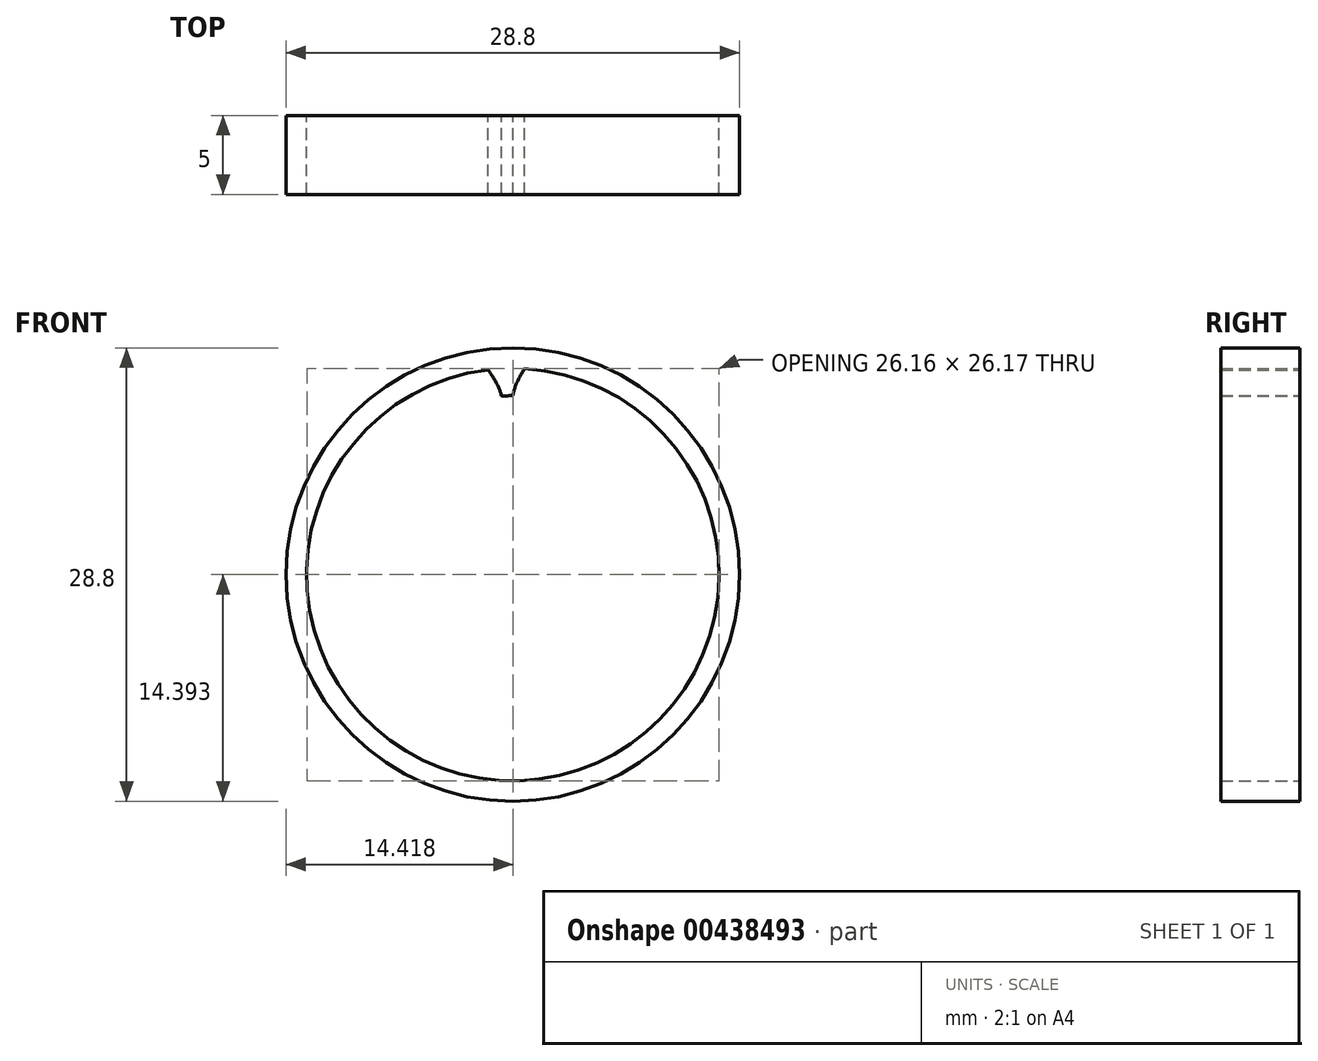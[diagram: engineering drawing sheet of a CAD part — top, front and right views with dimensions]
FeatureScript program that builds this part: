
annotation { "Feature Type Name" : "Feature", "Feature Type Description" : "" }
export const myFeature = defineFeature(function(context is Context, id is Id, definition is map)
    precondition{}
    {
        {
            var Q0;
            Q0=qCreatedBy(makeId("Front.planeOp"),FACE);
            var sketch = newSketch(context, id + "F0", { "sketchPlane" : qUnion([Q0])});
            skCircle(sketch, "E0", {"center": v(0, 0) * mm, "radius": 11.28 * mm, "construction": true});
            skLineSegment(sketch, "E1", {"start": v(1.96, 11.1) * mm, "end": v(0.02, 11.45) * mm, "construction": true});
            skLineSegment(sketch, "E2", {"start": v(0, 0) * mm, "end": v(0, 11.28) * mm, "construction": true});
            skLineSegment(sketch, "E3", {"start": v(1.96, 11.1) * mm, "end": v(0, 0) * mm, "construction": true});
            skLineSegment(sketch, "E4", {"start": v(0, 0) * mm, "end": v(3.86, 10.6) * mm, "construction": true});
            skLineSegment(sketch, "E5", {"start": v(3.86, 10.6) * mm, "end": v(2, 11.27) * mm, "construction": true});
            skLineSegment(sketch, "E6", {"start": v(0, 0) * mm, "end": v(5.64, 9.77) * mm, "construction": true});
            skLineSegment(sketch, "E7", {"start": v(5.64, 9.77) * mm, "end": v(3.93, 10.75) * mm, "construction": true});
            skLineSegment(sketch, "E8", {"start": v(0, 0) * mm, "end": v(7.25, 8.64) * mm, "construction": true});
            skLineSegment(sketch, "E9", {"start": v(7.25, 8.64) * mm, "end": v(5.74, 9.9) * mm, "construction": true});
            skLineSegment(sketch, "E10", {"start": v(2, 11.27) * mm, "end": v(0.16, 11.94) * mm, "construction": true});
            skLineSegment(sketch, "E11", {"start": v(3.93, 10.75) * mm, "end": v(2.23, 11.73) * mm, "construction": true});
            skLineSegment(sketch, "E12", {"start": v(2.23, 11.73) * mm, "end": v(0.52, 12.72) * mm, "construction": true});
            skLineSegment(sketch, "E13", {"start": v(5.74, 9.9) * mm, "end": v(4.23, 11.17) * mm, "construction": true});
            skLineSegment(sketch, "E14", {"start": v(4.23, 11.17) * mm, "end": v(2.73, 12.43) * mm, "construction": true});
            skLineSegment(sketch, "E15", {"start": v(2.73, 12.43) * mm, "end": v(1.22, 13.7) * mm, "construction": true});
            skFitSpline(sketch, "E16", {"points": [v(1.22, 13.7) * mm, v(0.52, 12.72) * mm, v(0.16, 11.94) * mm, v(0.02, 11.45) * mm, v(0, 11.28) * mm], "startDerivative": vector(-2.58, -3.18) * mm, "endDerivative": vector(0, -0.66) * mm});
            skLineSegment(sketch, "E17", {"start": v(0.02, 11.45) * mm, "end": v(-0.01, 11.28) * mm, "construction": true});
            skLineSegment(sketch, "E18", {"start": v(0.16, 11.94) * mm, "end": v(-0.08, 11.28) * mm, "construction": true});
            skLineSegment(sketch, "E19", {"start": v(0.52, 12.72) * mm, "end": v(-0.3, 11.27) * mm, "construction": true});
            skCircle(sketch, "E20", {"center": v(0, 0) * mm, "radius": 13.1 * mm});
            skCircle(sketch, "E21", {"center": v(0, 0) * mm, "radius": 12 * mm, "construction": true});
            skCircle(sketch, "E22", {"center": v(0, 0) * mm, "radius": 11.36 * mm});
            skLineSegment(sketch, "E23", {"start": v(0, 0) * mm, "end": v(0.18, 12) * mm, "construction": true});
            skLineSegment(sketch, "E24", {"start": v(-0.38, 12) * mm, "end": v(0, 0) * mm, "construction": true});
            skFitSpline(sketch, "E25.MirrorCS", {"points": [v(-2.08, 13.6) * mm, v(-1.33, 12.66) * mm, v(-0.91, 11.9) * mm, v(-0.74, 11.42) * mm, v(-0.71, 11.25) * mm], "startDerivative": vector(2.78, -3.01) * mm, "endDerivative": vector(0.04, -0.65) * mm});
            skCircle(sketch, "E26", {"center": v(0, 0) * mm, "radius": 14.4 * mm});
            skSolve(sketch);
        }
        {
            var Q0;
            Q0=makeQuery(id+"F0.imprint","IMPRINT",FACE,{"disambiguationData":[TD([[makeQuery(id+"F0.imprint","IMPRINT",EDGE,{"derivedFrom":sQuery(id+"F0.wireOp",EDGE,"E26")}),1.0]])]});
            extrude(context, id + "F1", {"entities" : qUnion([Q0]), "depth" : 5 * mm});
        }
        {
            var Q0;
            {var subQ0=sQuery(id+"F0.wireOp",EDGE,"E20");var subQ1=sQuery(id+"F0.wireOp",EDGE,"E16");var subQ2=makeQuery(id+"F0.imprint","INTERSECT",VERTEX,{"derivedFrom":[subQ1,subQ0]});Q0=makeQuery(id+"F0.imprint","IMPRINT",FACE,{"disambiguationData":[TD([[makeQuery(id+"F0.imprint","IMPRINT",EDGE,{"disambiguationData":[TD([[subQ2,-1.0]])],"derivedFrom":subQ1}),-1.0]])]});}
            extrude(context, id + "F2", {"entities" : qUnion([Q0]), "operationType" : NewBodyOperationType.ADD, "depth" : 5 * mm});
        }
    });
